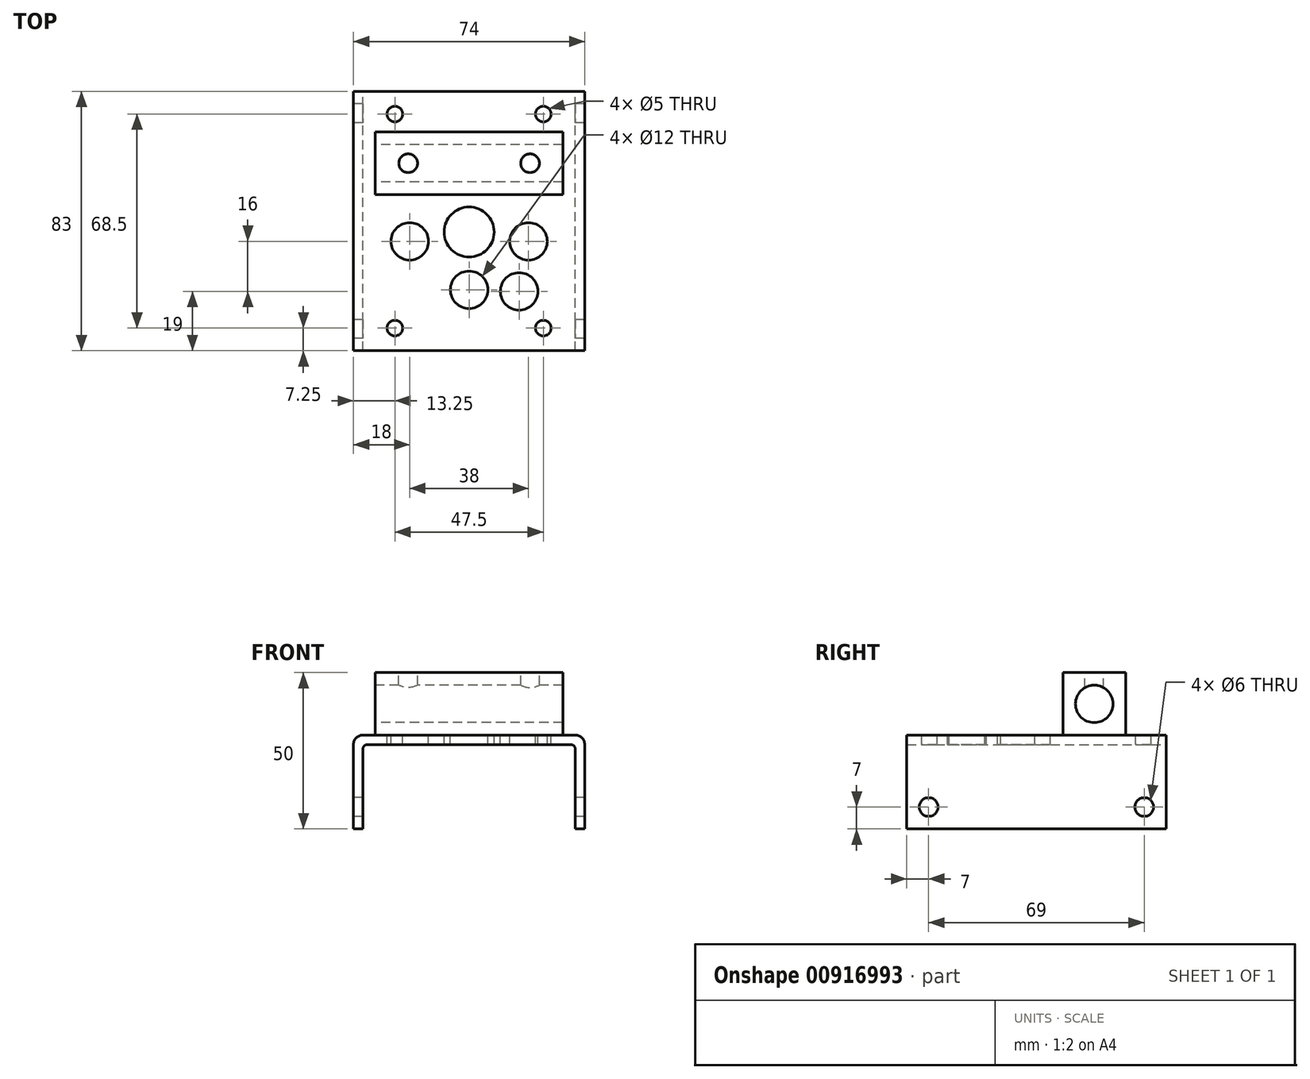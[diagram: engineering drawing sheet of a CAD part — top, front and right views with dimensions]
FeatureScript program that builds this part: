
annotation { "Feature Type Name" : "Feature", "Feature Type Description" : "" }
export const myFeature = defineFeature(function(context is Context, id is Id, definition is map)
    precondition{}
    {
        {
            var Q0;
            Q0=qCreatedBy(makeId("Front.planeOp"),FACE);
            var sketch = newSketch(context, id + "F0", { "sketchPlane" : qUnion([Q0])});
            skLineSegment(sketch, "E0.bottom", {"start": v(0, 0) * mm, "end": v(3, 0) * mm});
            skLineSegment(sketch, "E0.top", {"start": v(3, 30) * mm, "end": v(71, 30) * mm});
            skLineSegment(sketch, "E0.left", {"start": v(0, 0) * mm, "end": v(0, 27) * mm});
            skLineSegment(sketch, "E0.right", {"start": v(74, 0) * mm, "end": v(74, 27) * mm});
            skLineSegment(sketch, "E1.0", {"start": v(4.5, 27) * mm, "end": v(69.5, 27) * mm});
            skLineSegment(sketch, "E2.0", {"start": v(3, 0) * mm, "end": v(3, 25.5) * mm});
            skLineSegment(sketch, "E3.0", {"start": v(71, 0) * mm, "end": v(71, 25.5) * mm});
            skLineSegment(sketch, "E4.trimOffspring", {"start": v(71, 0) * mm, "end": v(74, 0) * mm});
            skPoint(sketch, "E5.visualSharp", {"position": v(0, 30) * mm});
            skArc(sketch, "E5.filletArc", {"start": v(3, 30) * mm, "mid": v(0.88, 29.12) * mm, "end": v(0, 27) * mm});
            skArc(sketch, "E6.filletArc", {"start": v(4.5, 27) * mm, "mid": v(3.44, 26.56) * mm, "end": v(3, 25.5) * mm});
            skPoint(sketch, "E7.visualSharp", {"position": v(71, 27) * mm});
            skArc(sketch, "E7.filletArc", {"start": v(71, 25.5) * mm, "mid": v(70.56, 26.56) * mm, "end": v(69.5, 27) * mm});
            skPoint(sketch, "E8.visualSharp", {"position": v(74, 30) * mm});
            skArc(sketch, "E8.filletArc", {"start": v(74, 27) * mm, "mid": v(73.12, 29.12) * mm, "end": v(71, 30) * mm});
            skSolve(sketch);
        }
        {
            var Q0;
            Q0=makeQuery(id+"F0.imprint","IMPRINT",FACE,{"disambiguationData":[TD([[makeQuery(id+"F0.imprint","IMPRINT",EDGE,{"derivedFrom":sQuery(id+"F0.wireOp",EDGE,"E0.bottom")}),1.0]])]});
            extrude(context, id + "F1", {"entities" : qUnion([Q0]), "depth" : 83 * mm, "offsetDistance" : 25 * mm});
        }
        {
            var Q0;
            Q0=makeQuery(id+"F1.opExtrude","SWEPT_FACE",FACE,{"disambiguationData":[OSD([sQuery(id+"F0.wireOp",EDGE,"E0.top")])]});
            var sketch = newSketch(context, id + "F2", { "sketchPlane" : qUnion([Q0])});
            skLineSegment(sketch, "E9.bottom", {"start": v(13.25, -75.75) * mm, "end": v(60.75, -75.75) * mm, "construction": true});
            skLineSegment(sketch, "E9.top", {"start": v(13.25, -7.25) * mm, "end": v(60.75, -7.25) * mm, "construction": true});
            skLineSegment(sketch, "E9.left", {"start": v(13.25, -75.75) * mm, "end": v(13.25, -7.25) * mm, "construction": true});
            skLineSegment(sketch, "E9.right", {"start": v(60.75, -75.75) * mm, "end": v(60.75, -7.25) * mm, "construction": true});
            skCircle(sketch, "E10", {"center": v(13.25, -7.25) * mm, "radius": 2.5 * mm});
            skCircle(sketch, "E11", {"center": v(60.75, -7.25) * mm, "radius": 2.5 * mm});
            skCircle(sketch, "E12", {"center": v(60.75, -75.75) * mm, "radius": 2.5 * mm});
            skCircle(sketch, "E13", {"center": v(13.25, -75.75) * mm, "radius": 2.5 * mm});
            skSolve(sketch);
        }
        {
            var Q0;
            Q0=makeQuery(id+"F2.imprint","IMPRINT",FACE,{"disambiguationData":[TD([[makeQuery(id+"F2.imprint","IMPRINT",EDGE,{"derivedFrom":sQuery(id+"F2.wireOp",EDGE,"E10")}),1.0]])]});
            var Q1;
            Q1=makeQuery(id+"F2.imprint","IMPRINT",FACE,{"disambiguationData":[TD([[makeQuery(id+"F2.imprint","IMPRINT",EDGE,{"derivedFrom":sQuery(id+"F2.wireOp",EDGE,"E11")}),1.0]])]});
            var Q2;
            Q2=makeQuery(id+"F2.imprint","IMPRINT",FACE,{"disambiguationData":[TD([[makeQuery(id+"F2.imprint","IMPRINT",EDGE,{"derivedFrom":sQuery(id+"F2.wireOp",EDGE,"E12")}),1.0]])]});
            var Q3;
            Q3=makeQuery(id+"F2.imprint","IMPRINT",FACE,{"disambiguationData":[TD([[makeQuery(id+"F2.imprint","IMPRINT",EDGE,{"derivedFrom":sQuery(id+"F2.wireOp",EDGE,"E13")}),1.0]])]});
            extrude(context, id + "F3", {"entities" : qUnion([Q0, Q1, Q2, Q3]), "operationType" : NewBodyOperationType.REMOVE, "endBound" : BoundingType.THROUGH_ALL, "oppositeDirection" : true, "depth" : 25 * mm, "offsetDistance" : 25 * mm});
        }
        {
            var Q0;
            Q0=makeQuery(id+"F1.opExtrude","SWEPT_FACE",FACE,{"disambiguationData":[OSD([sQuery(id+"F0.wireOp",EDGE,"E0.top")])]});
            var sketch = newSketch(context, id + "F4", { "sketchPlane" : qUnion([Q0])});
            skCircle(sketch, "E14", {"center": v(53, -64) * mm, "radius": 6 * mm});
            skCircle(sketch, "E15", {"center": v(37, -63.5) * mm, "radius": 6 * mm});
            skCircle(sketch, "E16", {"center": v(56, -48) * mm, "radius": 6 * mm});
            skCircle(sketch, "E17", {"center": v(18, -48) * mm, "radius": 6 * mm});
            skCircle(sketch, "E18", {"center": v(37, -45) * mm, "radius": 8 * mm});
            skSolve(sketch);
        }
        {
            var Q0;
            Q0=makeQuery(id+"F4.imprint","IMPRINT",FACE,{"disambiguationData":[TD([[makeQuery(id+"F4.imprint","IMPRINT",EDGE,{"derivedFrom":sQuery(id+"F4.wireOp",EDGE,"E18")}),1.0]])]});
            var Q1;
            Q1=makeQuery(id+"F4.imprint","IMPRINT",FACE,{"disambiguationData":[TD([[makeQuery(id+"F4.imprint","IMPRINT",EDGE,{"derivedFrom":sQuery(id+"F4.wireOp",EDGE,"E16")}),1.0]])]});
            var Q2;
            Q2=makeQuery(id+"F4.imprint","IMPRINT",FACE,{"disambiguationData":[TD([[makeQuery(id+"F4.imprint","IMPRINT",EDGE,{"derivedFrom":sQuery(id+"F4.wireOp",EDGE,"E14")}),1.0]])]});
            var Q3;
            Q3=makeQuery(id+"F4.imprint","IMPRINT",FACE,{"disambiguationData":[TD([[makeQuery(id+"F4.imprint","IMPRINT",EDGE,{"derivedFrom":sQuery(id+"F4.wireOp",EDGE,"E15")}),1.0]])]});
            var Q4;
            Q4=makeQuery(id+"F4.imprint","IMPRINT",FACE,{"disambiguationData":[TD([[makeQuery(id+"F4.imprint","IMPRINT",EDGE,{"derivedFrom":sQuery(id+"F4.wireOp",EDGE,"E17")}),1.0]])]});
            extrude(context, id + "F5", {"entities" : qUnion([Q0, Q1, Q2, Q3, Q4]), "operationType" : NewBodyOperationType.REMOVE, "endBound" : BoundingType.THROUGH_ALL, "oppositeDirection" : true, "depth" : 25 * mm, "offsetDistance" : 25 * mm});
        }
        {
            var Q0;
            Q0=makeQuery(id+"F1.opExtrude","SWEPT_FACE",FACE,{"disambiguationData":[OSD([sQuery(id+"F0.wireOp",EDGE,"E0.left")])]});
            var sketch = newSketch(context, id + "F6", { "sketchPlane" : qUnion([Q0])});
            skCircle(sketch, "E19", {"center": v(76, 7) * mm, "radius": 3 * mm});
            skCircle(sketch, "E20", {"center": v(7, 7) * mm, "radius": 3 * mm});
            skSolve(sketch);
        }
        {
            var Q0;
            Q0=makeQuery(id+"F6.imprint","IMPRINT",FACE,{"disambiguationData":[TD([[makeQuery(id+"F6.imprint","IMPRINT",EDGE,{"derivedFrom":sQuery(id+"F6.wireOp",EDGE,"E20")}),1.0]])]});
            var Q1;
            Q1=makeQuery(id+"F6.imprint","IMPRINT",FACE,{"disambiguationData":[TD([[makeQuery(id+"F6.imprint","IMPRINT",EDGE,{"derivedFrom":sQuery(id+"F6.wireOp",EDGE,"E19")}),1.0]])]});
            extrude(context, id + "F7", {"entities" : qUnion([Q0, Q1]), "operationType" : NewBodyOperationType.REMOVE, "endBound" : BoundingType.THROUGH_ALL, "oppositeDirection" : true, "depth" : 25 * mm, "offsetDistance" : 25 * mm});
        }
        {
            var Q0;
            Q0=makeQuery(id+"F1.opExtrude","SWEPT_FACE",FACE,{"disambiguationData":[OSD([sQuery(id+"F0.wireOp",EDGE,"E0.top")])]});
            var sketch = newSketch(context, id + "F8", { "sketchPlane" : qUnion([Q0])});
            skLineSegment(sketch, "E21.bottom", {"start": v(7, -13) * mm, "end": v(67, -13) * mm});
            skLineSegment(sketch, "E21.top", {"start": v(7, -33) * mm, "end": v(67, -33) * mm});
            skLineSegment(sketch, "E21.left", {"start": v(7, -13) * mm, "end": v(7, -33) * mm});
            skLineSegment(sketch, "E21.right", {"start": v(67, -13) * mm, "end": v(67, -33) * mm});
            skSolve(sketch);
        }
        {
            var Q0;
            Q0=makeQuery(id+"F8.imprint","IMPRINT",FACE,{"disambiguationData":[TD([[makeQuery(id+"F8.imprint","IMPRINT",EDGE,{"derivedFrom":sQuery(id+"F8.wireOp",EDGE,"E21.bottom")}),-1.0]])]});
            extrude(context, id + "F9", {"entities" : qUnion([Q0]), "operationType" : NewBodyOperationType.ADD, "depth" : 20 * mm, "offsetDistance" : 25 * mm});
        }
        {
            var Q0;
            Q0=makeQuery(id+"F9.opExtrude","SWEPT_FACE",FACE,{"disambiguationData":[OSD([sQuery(id+"F8.wireOp",EDGE,"E21.left")])]});
            var sketch = newSketch(context, id + "F10", { "sketchPlane" : qUnion([Q0])});
            skCircle(sketch, "E22", {"center": v(23, 40) * mm, "radius": 6 * mm});
            skPoint(sketch, "E22.centerSnap0", {"position": v(23, 50) * mm});
            skPoint(sketch, "E22.centerSnap1", {"position": v(33, 40) * mm});
            skSolve(sketch);
        }
        {
            var Q0;
            Q0=makeQuery(id+"F10.imprint","IMPRINT",FACE,{"disambiguationData":[TD([[makeQuery(id+"F10.imprint","IMPRINT",EDGE,{"derivedFrom":sQuery(id+"F10.wireOp",EDGE,"E22")}),1.0]])]});
            extrude(context, id + "F11", {"entities" : qUnion([Q0]), "operationType" : NewBodyOperationType.REMOVE, "endBound" : BoundingType.THROUGH_ALL, "oppositeDirection" : true, "depth" : 25 * mm, "offsetDistance" : 25 * mm});
        }
        {
            var Q0;
            Q0=makeQuery(id+"F9.opExtrude","CAP_FACE",FACE,{"disambiguationData":[OSD([sQuery(id+"F8.wireOp",EDGE,"E21.bottom"),sQuery(id+"F8.wireOp",EDGE,"E21.top"),sQuery(id+"F8.wireOp",EDGE,"E21.left"),sQuery(id+"F8.wireOp",EDGE,"E21.right")])],"isStart":false});
            var sketch = newSketch(context, id + "F12", { "sketchPlane" : qUnion([Q0])});
            skCircle(sketch, "E23", {"center": v(17.5, -23) * mm, "radius": 3 * mm});
            skPoint(sketch, "E23.centerSnap0", {"position": v(7, -23) * mm});
            skCircle(sketch, "E24", {"center": v(56.5, -23) * mm, "radius": 3 * mm});
            skSolve(sketch);
        }
        {
            var Q0;
            Q0=makeQuery(id+"F12.imprint","IMPRINT",FACE,{"disambiguationData":[TD([[makeQuery(id+"F12.imprint","IMPRINT",EDGE,{"derivedFrom":sQuery(id+"F12.wireOp",EDGE,"E23")}),1.0]])]});
            var Q1;
            Q1=makeQuery(id+"F12.imprint","IMPRINT",FACE,{"disambiguationData":[TD([[makeQuery(id+"F12.imprint","IMPRINT",EDGE,{"derivedFrom":sQuery(id+"F12.wireOp",EDGE,"E24")}),1.0]])]});
            extrude(context, id + "F13", {"entities" : qUnion([Q0, Q1]), "operationType" : NewBodyOperationType.REMOVE, "endBound" : BoundingType.UP_TO_NEXT, "oppositeDirection" : true, "depth" : 25 * mm, "offsetDistance" : 25 * mm});
        }
    });
